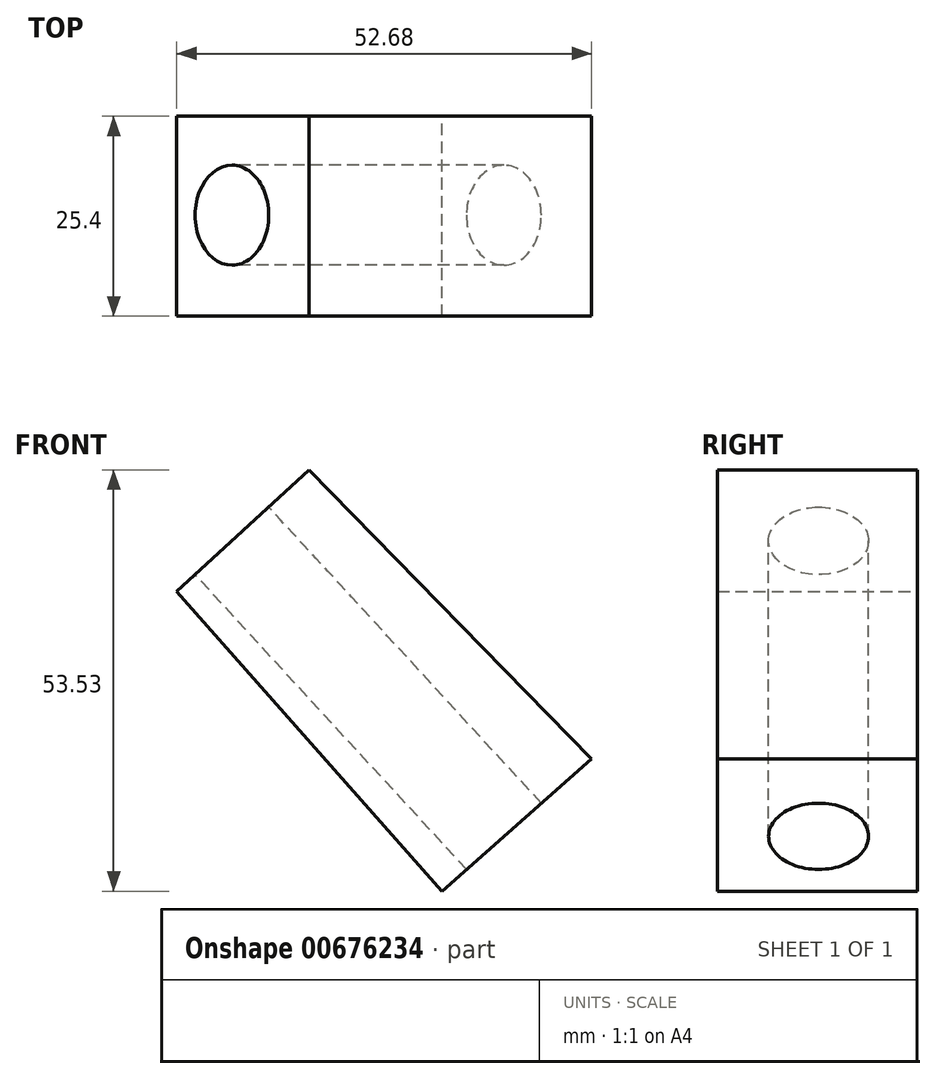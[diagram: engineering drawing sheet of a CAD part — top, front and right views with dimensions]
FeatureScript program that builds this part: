
annotation { "Feature Type Name" : "Feature", "Feature Type Description" : "" }
export const myFeature = defineFeature(function(context is Context, id is Id, definition is map)
    precondition{}
    {
        {
            var Q0;
            Q0=qCreatedBy(makeId("Front.planeOp"),FACE);
            var sketch = newSketch(context, id + "F0", { "sketchPlane" : qUnion([Q0])});
            skLineSegment(sketch, "E0", {"start": v(-33.66, 12.86) * mm, "end": v(0, -25.18) * mm});
            skLineSegment(sketch, "E1", {"start": v(0, -25.18) * mm, "end": v(19.02, -8.35) * mm});
            skLineSegment(sketch, "E2", {"start": v(19.02, -8.35) * mm, "end": v(-16.84, 28.35) * mm});
            skLineSegment(sketch, "E3", {"start": v(-16.84, 28.35) * mm, "end": v(-33.66, 12.86) * mm});
            skSolve(sketch);
        }
        {
            var Q0;
            Q0=makeQuery(id+"F0.imprint","IMPRINT",FACE,{"disambiguationData":[TD([[makeQuery(id+"F0.imprint","IMPRINT",EDGE,{"derivedFrom":sQuery(id+"F0.wireOp",EDGE,"E0")}),1.0]])]});
            extrude(context, id + "F1", {"entities" : qUnion([Q0]), "depth" : 25.4 * mm, "offsetDistance" : 25.4 * mm});
        }
        {
            var Q0;
            Q0=makeQuery(id+"F1.opExtrude","SWEPT_FACE",FACE,{"disambiguationData":[OSD([sQuery(id+"F0.wireOp",EDGE,"E3")])]});
            var sketch = newSketch(context, id + "F2", { "sketchPlane" : qUnion([Q0])});
            skCircle(sketch, "E4", {"center": v(-6.53, -12.56) * mm, "radius": 6.35 * mm});
            skSolve(sketch);
        }
        {
            var Q0;
            Q0=makeQuery(id+"F2.imprint","IMPRINT",FACE,{"disambiguationData":[TD([[makeQuery(id+"F2.imprint","IMPRINT",EDGE,{"derivedFrom":sQuery(id+"F2.wireOp",EDGE,"E4")}),1.0]])]});
            extrude(context, id + "F3", {"entities" : qUnion([Q0]), "operationType" : NewBodyOperationType.REMOVE, "endBound" : BoundingType.THROUGH_ALL, "oppositeDirection" : true, "depth" : 25.4 * mm, "offsetDistance" : 25.4 * mm});
        }
    });
